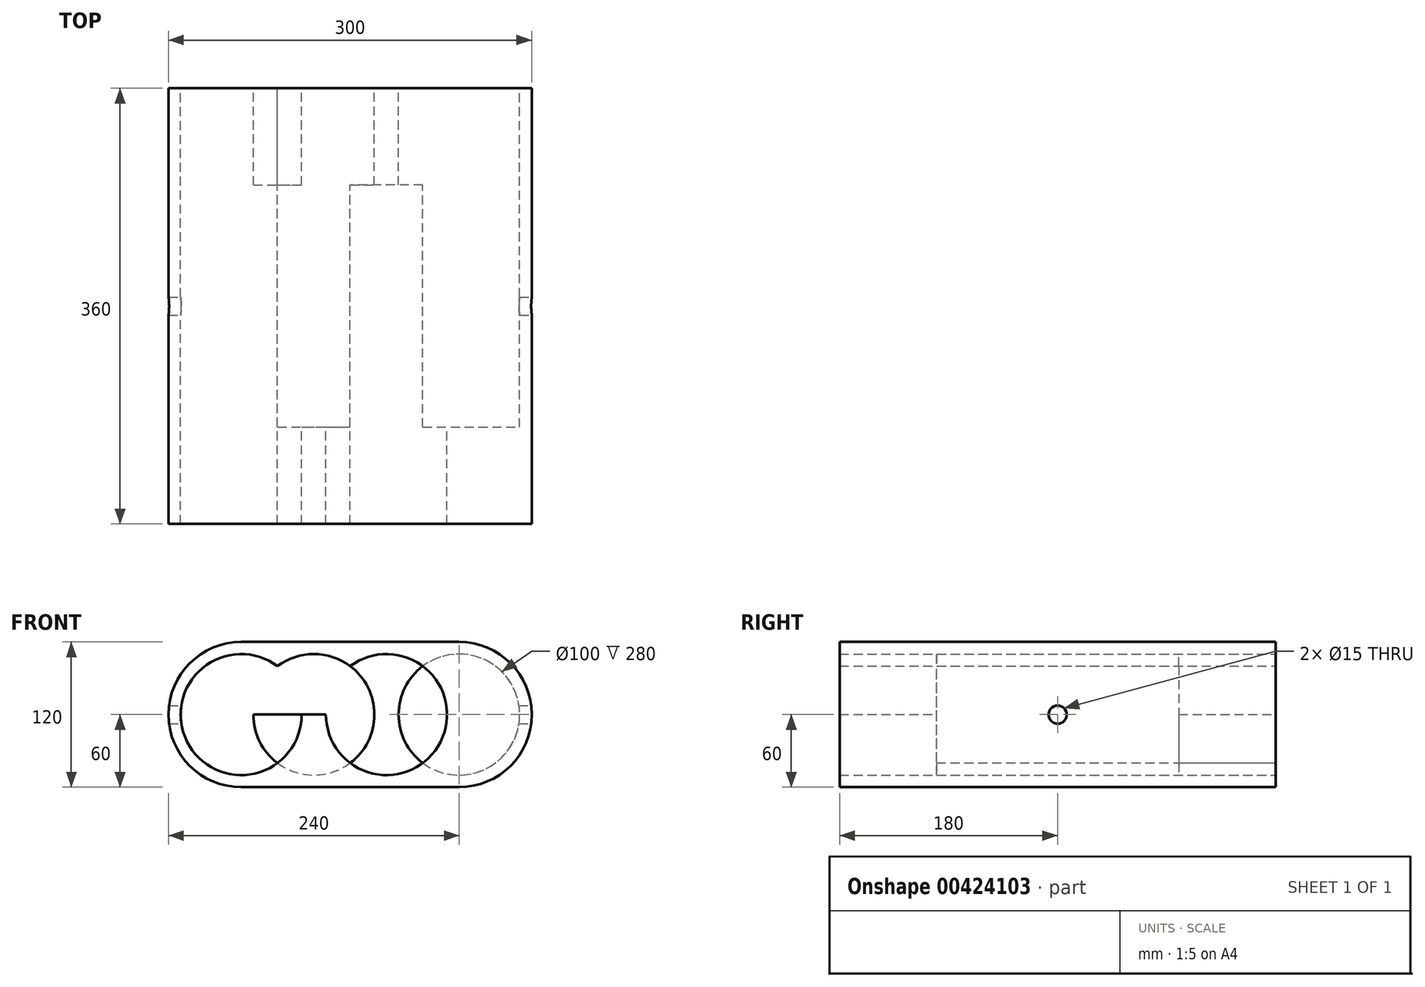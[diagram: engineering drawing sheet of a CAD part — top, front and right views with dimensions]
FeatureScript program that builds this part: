
annotation { "Feature Type Name" : "Feature", "Feature Type Description" : "" }
export const myFeature = defineFeature(function(context is Context, id is Id, definition is map)
    precondition{}
    {
        {
            var Q0;
            Q0=qCreatedBy(makeId("Front.planeOp"),FACE);
            var sketch = newSketch(context, id + "F0", { "sketchPlane" : qUnion([Q0])});
            skCircle(sketch, "E0", {"center": v(0, 0) * mm, "radius": 50 * mm});
            skCircle(sketch, "E1", {"center": v(180, 0) * mm, "radius": 50 * mm});
            skArc(sketch, "E2", {"start": v(0, 60) * mm, "mid": v(-60, 0) * mm, "end": v(0, -60) * mm});
            skArc(sketch, "E3", {"start": v(180, -60) * mm, "mid": v(240, 0) * mm, "end": v(180, 60) * mm});
            skLineSegment(sketch, "E4", {"start": v(0, 60) * mm, "end": v(180, 60) * mm});
            skLineSegment(sketch, "E5", {"start": v(0, -60) * mm, "end": v(180, -60) * mm});
            skCircle(sketch, "E6", {"center": v(60, 0) * mm, "radius": 50 * mm});
            skCircle(sketch, "E7", {"center": v(120, 0) * mm, "radius": 50 * mm});
            skLineSegment(sketch, "E8", {"start": v(0, 0) * mm, "end": v(60, 0) * mm});
            skLineSegment(sketch, "E9", {"start": v(60, 0) * mm, "end": v(120, 0) * mm});
            skLineSegment(sketch, "E10", {"start": v(120, 0) * mm, "end": v(180, 0) * mm});
            skSolve(sketch);
        }
        {
            var Q0;
            Q0 = qSketchRegion(id + "F0", true);
            extrude(context, id + "F1", {"entities" : qUnion([Q0]), "depth" : 360 * mm});
        }
        {
            var Q0;
            Q0=qCreatedBy(makeId("Right.planeOp"),FACE);
            var sketch = newSketch(context, id + "F2", { "sketchPlane" : qUnion([Q0])});
            skLineSegment(sketch, "E11", {"start": v(0, 0) * mm, "end": v(-360, 0) * mm, "construction": true});
            skCircle(sketch, "E12", {"center": v(-180, 0) * mm, "radius": 7.5 * mm});
            skSolve(sketch);
        }
        {
            var Q0;
            Q0 = qSketchRegion(id + "F2", true);
            extrude(context, id + "F3", {"entities" : qUnion([Q0]), "operationType" : NewBodyOperationType.REMOVE, "endBound" : BoundingType.THROUGH_ALL, "oppositeDirection" : true, "depth" : 25 * mm, "hasSecondDirection" : true, "secondDirectionBound" : SecondDirectionBoundingType.THROUGH_ALL, "secondDirectionOppositeDirection" : false, "secondDirectionDepth" : 25 * mm});
        }
        {
            var Q0;
            {var subQ3=sQuery(id+"F0.wireOp",EDGE,"E0");var subQ6=sQuery(id+"F0.wireOp",EDGE,"E6");var subQ9=makeQuery(id+"F0.imprint","INTERSECT",VERTEX,{"disambiguationData":[OD(0.0)],"derivedFrom":[subQ3,subQ6]});Q0=makeQuery(id+"F0.imprint","IMPRINT",FACE,{"disambiguationData":[TD([[makeQuery(id+"F0.imprint","IMPRINT",EDGE,{"disambiguationData":[TD([[subQ9,1.0]])],"derivedFrom":subQ3}),-1.0]])]});}
            var Q1;
            {var subQ1=sQuery(id+"F0.wireOp",EDGE,"E8");var subQ3=sQuery(id+"F0.wireOp",EDGE,"E0");var subQ4=makeQuery(id+"F0.imprint","INTERSECT",VERTEX,{"derivedFrom":[subQ3,subQ1]});Q1=makeQuery(id+"F0.imprint","IMPRINT",FACE,{"disambiguationData":[TD([[makeQuery(id+"F0.imprint","IMPRINT",EDGE,{"disambiguationData":[TD([[subQ4,1.0]])],"derivedFrom":subQ3}),-1.0]])]});}
            var Q2;
            {var subQ0=sQuery(id+"F0.wireOp",EDGE,"E7");var subQ1=sQuery(id+"F0.wireOp",EDGE,"E1");var subQ2=makeQuery(id+"F0.imprint","INTERSECT",VERTEX,{"disambiguationData":[OD(0.0)],"derivedFrom":[subQ1,subQ0]});Q2=makeQuery(id+"F0.imprint","IMPRINT",FACE,{"disambiguationData":[TD([[makeQuery(id+"F0.imprint","IMPRINT",EDGE,{"disambiguationData":[TD([[subQ2,1.0]])],"derivedFrom":subQ1}),1.0]])]});}
            var Q3;
            Q3=makeQuery(id+"F1.opExtrude","CAP_FACE",FACE,{"disambiguationData":[OSD([sQuery(id+"F0.wireOp",EDGE,"E0"),sQuery(id+"F0.wireOp",EDGE,"E1"),sQuery(id+"F0.wireOp",EDGE,"E2"),sQuery(id+"F0.wireOp",EDGE,"E3"),sQuery(id+"F0.wireOp",EDGE,"E4"),sQuery(id+"F0.wireOp",EDGE,"E5"),sQuery(id+"F0.wireOp",EDGE,"E6"),sQuery(id+"F0.wireOp",EDGE,"E7")])],"isStart":false});
            extrude(context, id + "F4", {"entities" : qUnion([Q0, Q1, Q2]), "operationType" : NewBodyOperationType.ADD, "endBound" : BoundingType.UP_TO_SURFACE, "endBoundEntityFace" : qUnion([Q3]), "depth" : 25 * mm, "hasSecondDirection" : true, "secondDirectionOppositeDirection" : false, "secondDirectionDepth" : 280 * mm});
        }
        {
            var Q0;
            {var subQ0=sQuery(id+"F0.wireOp",EDGE,"E6");var subQ1=sQuery(id+"F0.wireOp",EDGE,"E0");var subQ2=makeQuery(id+"F0.imprint","INTERSECT",VERTEX,{"disambiguationData":[OD(0.0)],"derivedFrom":[subQ1,subQ0]});Q0=makeQuery(id+"F0.imprint","IMPRINT",FACE,{"disambiguationData":[TD([[makeQuery(id+"F0.imprint","IMPRINT",EDGE,{"disambiguationData":[TD([[subQ2,-1.0]])],"derivedFrom":subQ1}),1.0]])]});}
            var Q1;
            {var subQ0=sQuery(id+"F0.wireOp",EDGE,"E10");var subQ6=sQuery(id+"F0.wireOp",EDGE,"E1");var subQ9=makeQuery(id+"F0.imprint","INTERSECT",VERTEX,{"derivedFrom":[subQ6,subQ0]});Q1=makeQuery(id+"F0.imprint","IMPRINT",FACE,{"disambiguationData":[TD([[makeQuery(id+"F0.imprint","IMPRINT",EDGE,{"disambiguationData":[TD([[subQ9,1.0]])],"derivedFrom":subQ6}),-1.0]])]});}
            var Q2;
            {var subQ0=sQuery(id+"F0.wireOp",EDGE,"E10");var subQ7=sQuery(id+"F0.wireOp",EDGE,"E1");var subQ8=makeQuery(id+"F0.imprint","INTERSECT",VERTEX,{"derivedFrom":[subQ7,subQ0]});Q2=makeQuery(id+"F0.imprint","IMPRINT",FACE,{"disambiguationData":[TD([[makeQuery(id+"F0.imprint","IMPRINT",EDGE,{"disambiguationData":[TD([[subQ8,-1.0]])],"derivedFrom":subQ7}),-1.0]])]});}
            extrude(context, id + "F5", {"entities" : qUnion([Q0, Q1, Q2]), "operationType" : NewBodyOperationType.ADD, "depth" : (360 - 280) * mm});
        }
    });
